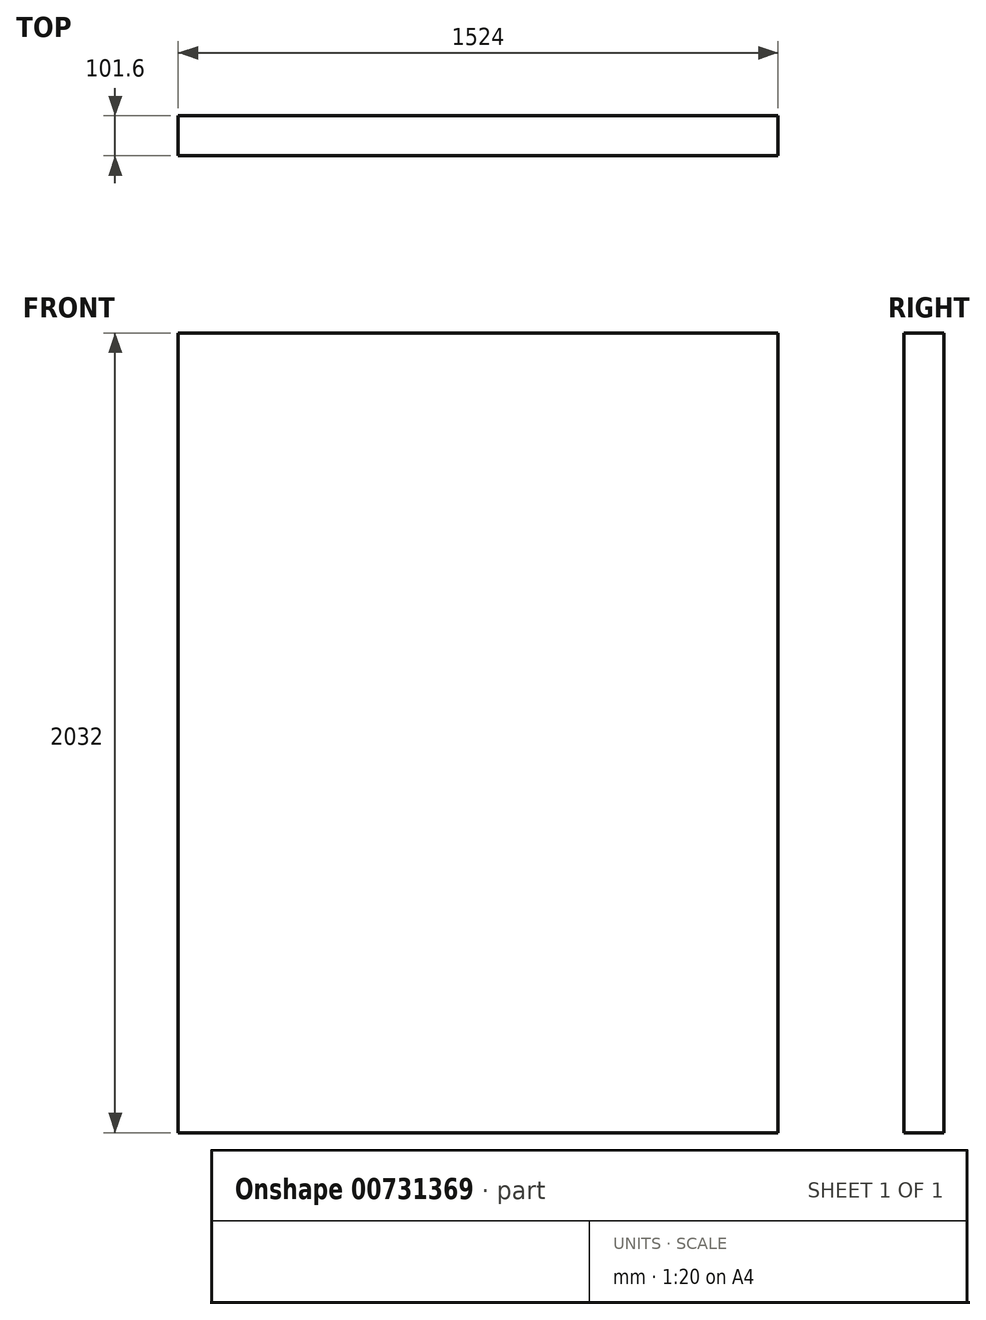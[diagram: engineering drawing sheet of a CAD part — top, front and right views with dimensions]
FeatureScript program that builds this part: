
annotation { "Feature Type Name" : "Feature", "Feature Type Description" : "" }
export const myFeature = defineFeature(function(context is Context, id is Id, definition is map)
    precondition{}
    {
        {
            var Q0;
            Q0=qCreatedBy(makeId("Front.planeOp"),FACE);
            var sketch = newSketch(context, id + "F0", { "sketchPlane" : qUnion([Q0])});
            skLineSegment(sketch, "E0.bottom", {"start": v(762, 1016) * mm, "end": v(-762, 1016) * mm});
            skLineSegment(sketch, "E0.top", {"start": v(762, -1016) * mm, "end": v(-762, -1016) * mm});
            skLineSegment(sketch, "E0.left", {"start": v(762, 1016) * mm, "end": v(762, -1016) * mm});
            skLineSegment(sketch, "E0.right", {"start": v(-762, 1016) * mm, "end": v(-762, -1016) * mm});
            skPoint(sketch, "E0.middle", {"position": v(0, 0) * mm});
            skSolve(sketch);
        }
        {
            var Q0;
            Q0 = qSketchRegion(id + "F0", true);
            extrude(context, id + "F1", {"entities" : qUnion([Q0]), "depth" : 101.6 * mm, "offsetDistance" : 25.4 * mm});
        }
    });
